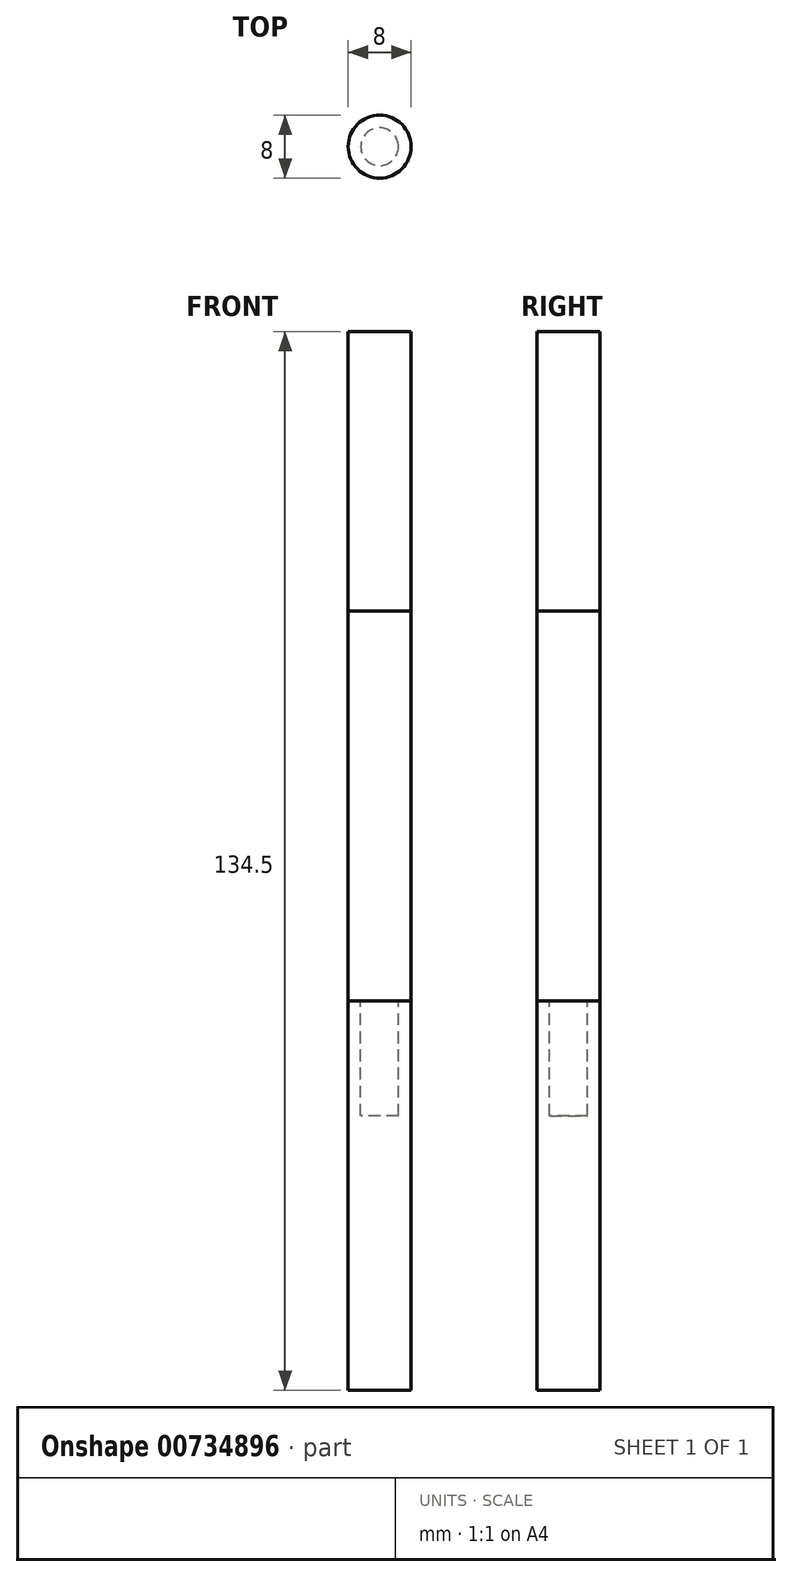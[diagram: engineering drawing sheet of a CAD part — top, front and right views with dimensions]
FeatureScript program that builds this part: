
annotation { "Feature Type Name" : "Feature", "Feature Type Description" : "" }
export const myFeature = defineFeature(function(context is Context, id is Id, definition is map)
    precondition{}
    {
        {
            var Q0;
            Q0=qCreatedBy(makeId("Top.planeOp"),FACE);
            var sketch = newSketch(context, id + "F0", { "sketchPlane" : qUnion([Q0])});
            skCircle(sketch, "E0", {"center": v(0, 0) * mm, "radius": 4 * mm});
            skCircle(sketch, "E1", {"center": v(0, 0) * mm, "radius": 2.4 * mm});
            skSolve(sketch);
        }
        {
            var Q0;
            Q0=makeQuery(id+"F0.imprint","IMPRINT",FACE,{"disambiguationData":[TD([[makeQuery(id+"F0.imprint","IMPRINT",EDGE,{"derivedFrom":sQuery(id+"F0.wireOp",EDGE,"E0")}),1.0]])]});
            var Q1;
            Q1=makeQuery(id+"F0.imprint","IMPRINT",FACE,{"disambiguationData":[TD([[makeQuery(id+"F0.imprint","IMPRINT",EDGE,{"derivedFrom":sQuery(id+"F0.wireOp",EDGE,"E1")}),1.0]])]});
            extrude(context, id + "F1", {"entities" : qUnion([Q0, Q1]), "depth" : 85 * mm, "offsetDistance" : 25 * mm});
        }
        {
            var Q0;
            Q0=makeQuery(id+"F0.imprint","IMPRINT",FACE,{"disambiguationData":[TD([[makeQuery(id+"F0.imprint","IMPRINT",EDGE,{"derivedFrom":sQuery(id+"F0.wireOp",EDGE,"E1")}),1.0]])]});
            extrude(context, id + "F2", {"entities" : qUnion([Q0]), "operationType" : NewBodyOperationType.ADD, "oppositeDirection" : true, "depth" : 14.6 * mm, "offsetDistance" : 25 * mm});
        }
        {
            var Q0;
            Q0=makeQuery(id+"F0.imprint","IMPRINT",FACE,{"disambiguationData":[TD([[makeQuery(id+"F0.imprint","IMPRINT",EDGE,{"derivedFrom":sQuery(id+"F0.wireOp",EDGE,"E1")}),1.0]])]});
            var Q1;
            Q1=makeQuery(id+"F0.imprint","IMPRINT",FACE,{"disambiguationData":[TD([[makeQuery(id+"F0.imprint","IMPRINT",EDGE,{"derivedFrom":sQuery(id+"F0.wireOp",EDGE,"E0")}),1.0]])]});
            extrude(context, id + "F3", {"entities" : qUnion([Q0, Q1]), "endBound" : BoundingType.SYMMETRIC, "depth" : 99 * mm, "offsetDistance" : 25 * mm});
        }
    });
